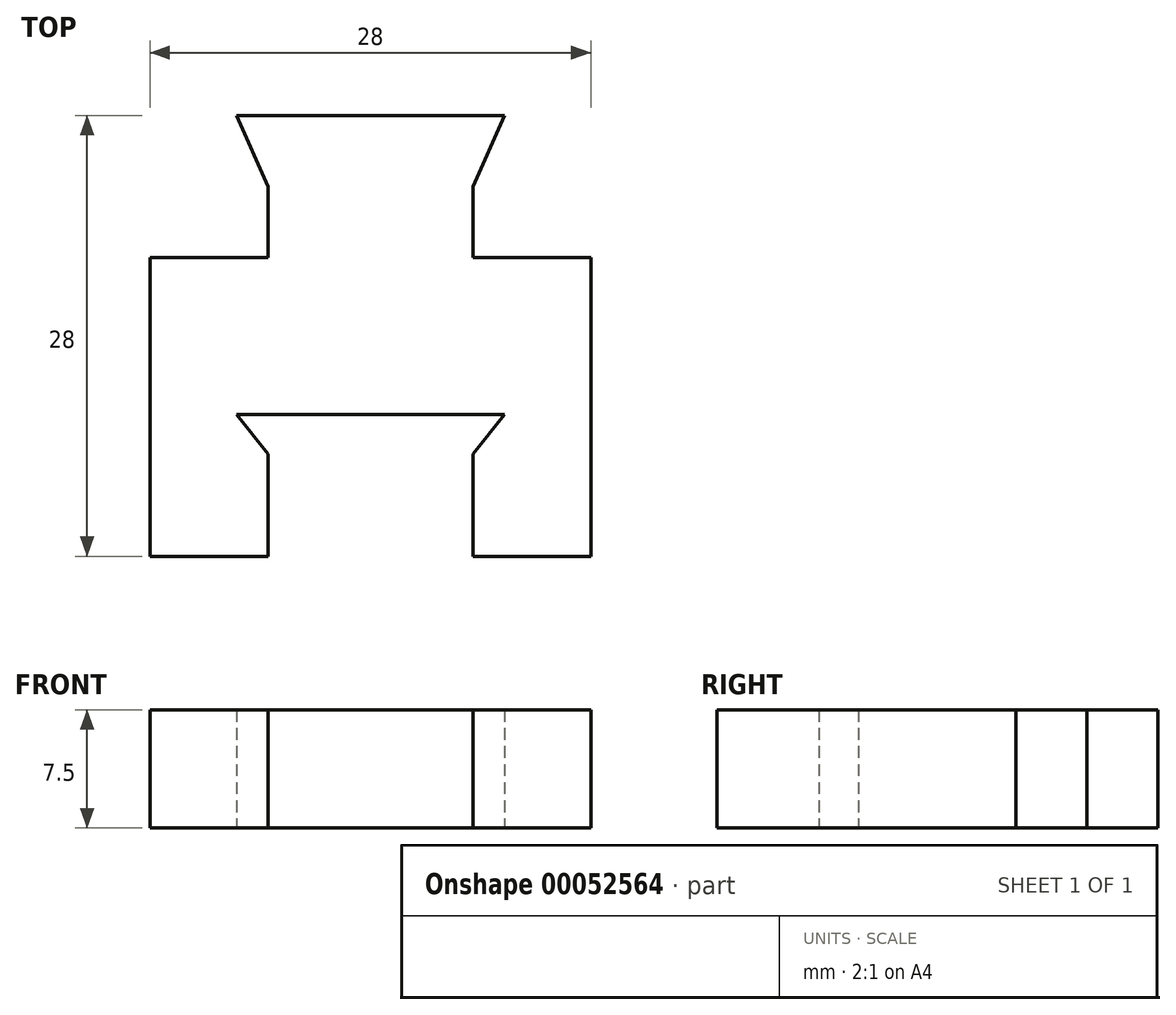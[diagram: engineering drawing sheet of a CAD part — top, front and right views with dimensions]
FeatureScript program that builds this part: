
annotation { "Feature Type Name" : "Feature", "Feature Type Description" : "" }
export const myFeature = defineFeature(function(context is Context, id is Id, definition is map)
    precondition{}
    {
        {
            var Q0;
            Q0=qCreatedBy(makeId("Top.planeOp"),FACE);
            var sketch = newSketch(context, id + "F0", { "sketchPlane" : qUnion([Q0])});
            skLineSegment(sketch, "E0.bottom", {"start": v(-39.92, -7.88) * mm, "end": v(-11.92, -7.88) * mm, "construction": true});
            skLineSegment(sketch, "E0.top", {"start": v(-39.92, -35.88) * mm, "end": v(-11.92, -35.88) * mm, "construction": true});
            skLineSegment(sketch, "E0.left", {"start": v(-39.92, -7.88) * mm, "end": v(-39.92, -35.88) * mm, "construction": true});
            skLineSegment(sketch, "E0.right", {"start": v(-11.92, -7.88) * mm, "end": v(-11.92, -35.88) * mm, "construction": true});
            skPoint(sketch, "E1", {"position": v(-11.92, -29.38) * mm});
            skPoint(sketch, "E2", {"position": v(-11.93, -26.88) * mm});
            skPoint(sketch, "E3", {"position": v(-11.92, -12.38) * mm});
            skPoint(sketch, "E4", {"position": v(-11.92, -16.88) * mm});
            skPoint(sketch, "E5", {"position": v(-39.92, -29.38) * mm});
            skPoint(sketch, "E6", {"position": v(-39.92, -26.88) * mm});
            skPoint(sketch, "E7", {"position": v(-39.92, -16.88) * mm});
            skPoint(sketch, "E8", {"position": v(-39.92, -12.38) * mm});
            skPoint(sketch, "E9", {"position": v(-32.42, -35.88) * mm});
            skPoint(sketch, "E10", {"position": v(-19.42, -35.88) * mm});
            skPoint(sketch, "E11", {"position": v(-34.42, -7.88) * mm});
            skPoint(sketch, "E12", {"position": v(-32.42, -7.88) * mm});
            skPoint(sketch, "E13", {"position": v(-19.42, -7.88) * mm});
            skPoint(sketch, "E14", {"position": v(-17.42, -7.88) * mm});
            skPoint(sketch, "E15", {"position": v(-34.42, -35.88) * mm});
            skPoint(sketch, "E16", {"position": v(-17.42, -35.88) * mm});
            skLineSegment(sketch, "E17", {"start": v(-34.42, -7.88) * mm, "end": v(-34.42, -35.88) * mm, "construction": true});
            skLineSegment(sketch, "E18", {"start": v(-32.42, -7.88) * mm, "end": v(-32.42, -35.88) * mm, "construction": true});
            skLineSegment(sketch, "E19", {"start": v(-19.42, -7.88) * mm, "end": v(-19.42, -35.88) * mm, "construction": true});
            skLineSegment(sketch, "E20", {"start": v(-17.42, -7.88) * mm, "end": v(-17.42, -35.88) * mm, "construction": true});
            skLineSegment(sketch, "E21", {"start": v(-39.92, -12.38) * mm, "end": v(-11.92, -12.38) * mm, "construction": true});
            skLineSegment(sketch, "E22", {"start": v(-39.92, -16.88) * mm, "end": v(-11.92, -16.88) * mm, "construction": true});
            skLineSegment(sketch, "E23", {"start": v(-39.92, -26.88) * mm, "end": v(-11.93, -26.88) * mm, "construction": true});
            skLineSegment(sketch, "E24", {"start": v(-39.92, -29.38) * mm, "end": v(-11.92, -29.38) * mm, "construction": true});
            skPoint(sketch, "E25", {"position": v(-34.42, -29.38) * mm});
            skPoint(sketch, "E26", {"position": v(-32.42, -29.38) * mm});
            skPoint(sketch, "E27", {"position": v(-19.42, -29.38) * mm});
            skPoint(sketch, "E28", {"position": v(-17.42, -29.38) * mm});
            skPoint(sketch, "E29", {"position": v(-17.42, -26.88) * mm});
            skPoint(sketch, "E30", {"position": v(-19.42, -26.88) * mm});
            skPoint(sketch, "E31", {"position": v(-32.42, -26.88) * mm});
            skPoint(sketch, "E32", {"position": v(-34.42, -26.88) * mm});
            skPoint(sketch, "E33", {"position": v(-34.42, -16.88) * mm});
            skPoint(sketch, "E34", {"position": v(-32.42, -16.88) * mm});
            skPoint(sketch, "E35", {"position": v(-19.42, -16.88) * mm});
            skPoint(sketch, "E36", {"position": v(-17.42, -16.88) * mm});
            skPoint(sketch, "E37", {"position": v(-17.42, -12.38) * mm});
            skPoint(sketch, "E38", {"position": v(-19.42, -12.38) * mm});
            skPoint(sketch, "E39", {"position": v(-32.42, -12.38) * mm});
            skPoint(sketch, "E40", {"position": v(-34.42, -12.38) * mm});
            skLineSegment(sketch, "E41", {"start": v(-32.42, -35.88) * mm, "end": v(-32.42, -29.38) * mm});
            skLineSegment(sketch, "E42", {"start": v(-34.42, -26.88) * mm, "end": v(-32.42, -29.38) * mm});
            skLineSegment(sketch, "E43", {"start": v(-34.42, -26.88) * mm, "end": v(-17.42, -26.88) * mm});
            skLineSegment(sketch, "E44", {"start": v(-17.42, -26.88) * mm, "end": v(-19.42, -29.38) * mm});
            skLineSegment(sketch, "E45", {"start": v(-19.42, -29.38) * mm, "end": v(-19.42, -35.88) * mm});
            skLineSegment(sketch, "E46", {"start": v(-32.42, -16.88) * mm, "end": v(-32.42, -12.38) * mm});
            skLineSegment(sketch, "E47", {"start": v(-32.42, -12.38) * mm, "end": v(-34.42, -7.88) * mm});
            skLineSegment(sketch, "E48", {"start": v(-34.42, -7.88) * mm, "end": v(-17.42, -7.88) * mm});
            skLineSegment(sketch, "E49", {"start": v(-17.42, -7.88) * mm, "end": v(-19.42, -12.38) * mm});
            skLineSegment(sketch, "E50", {"start": v(-19.42, -16.88) * mm, "end": v(-19.42, -12.38) * mm});
            skLineSegment(sketch, "E51", {"start": v(-32.42, -35.88) * mm, "end": v(-39.92, -35.88) * mm});
            skLineSegment(sketch, "E52", {"start": v(-39.92, -35.88) * mm, "end": v(-39.92, -16.88) * mm});
            skLineSegment(sketch, "E53", {"start": v(-39.92, -16.88) * mm, "end": v(-32.42, -16.88) * mm});
            skLineSegment(sketch, "E54", {"start": v(-19.42, -35.88) * mm, "end": v(-11.92, -35.88) * mm});
            skLineSegment(sketch, "E55", {"start": v(-11.92, -35.88) * mm, "end": v(-11.92, -16.88) * mm});
            skLineSegment(sketch, "E56", {"start": v(-11.92, -16.88) * mm, "end": v(-19.42, -16.88) * mm});
            skSolve(sketch);
        }
        {
            var Q0;
            Q0 = qSketchRegion(id + "F0", true);
            extrude(context, id + "F1", {"entities" : qUnion([Q0]), "depth" : 7.5 * mm});
        }
    });
